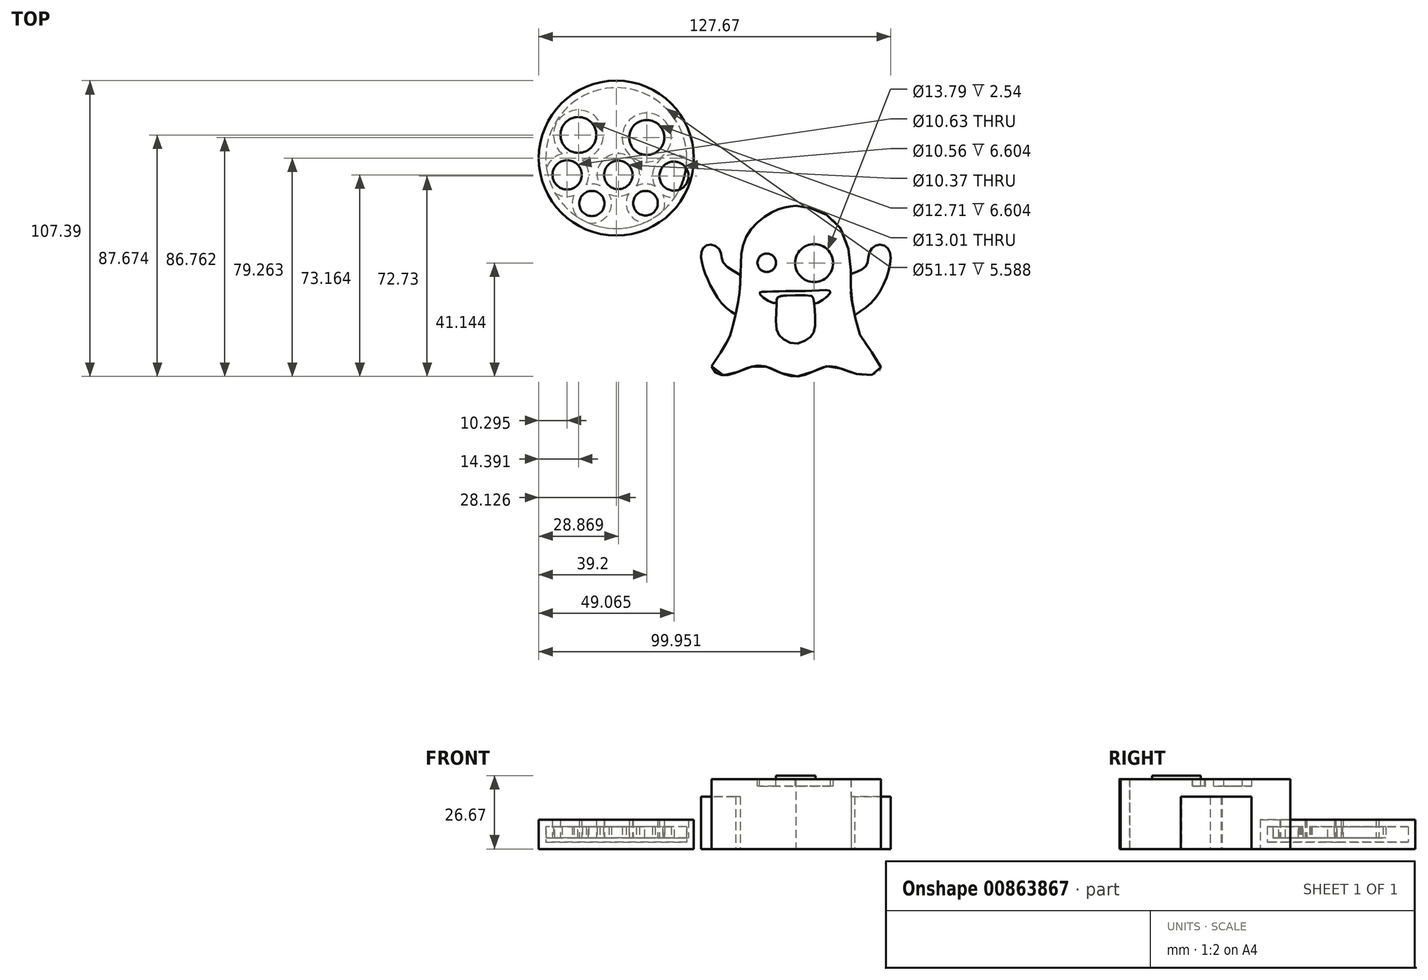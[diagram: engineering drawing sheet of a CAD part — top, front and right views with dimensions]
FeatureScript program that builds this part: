
annotation { "Feature Type Name" : "Feature", "Feature Type Description" : "" }
export const myFeature = defineFeature(function(context is Context, id is Id, definition is map)
    precondition{}
    {
        {
            var Q0;
            Q0=qCreatedBy(makeId("Top.planeOp"),FACE);
            var sketch = newSketch(context, id + "F0", { "sketchPlane" : qUnion([Q0])});
            skFitSpline(sketch, "E0", {"points": [v(0, 33.37) * mm, v(-7.03, 31.69) * mm, v(-18.14, 21.85) * mm, v(-20.2, 4.64) * mm, v(-22.78, -10) * mm, v(-30.58, -24.95) * mm], "startDerivative": vector(-46.08, -6.92) * mm, "endDerivative": vector(-91.46, -132.61) * mm});
            skFitSpline(sketch, "E1", {"points": [v(-30.58, -24.95) * mm, v(-24.72, -28.16) * mm, v(-17.9, -25.74) * mm, v(-11.49, -24.95) * mm, v(-3.25, -28.24) * mm, v(4.42, -27.74) * mm, v(11.56, -24.95) * mm, v(18.87, -26.78) * mm, v(26.52, -28.24) * mm, v(30.85, -25.7) * mm, v(24.56, -15.85) * mm, v(21.42, -6.6) * mm, v(19.97, 1.7) * mm, v(19.99, 10.33) * mm, v(16.2, 25.2) * mm, v(7.47, 31.76) * mm, v(0, 33.37) * mm], "startDerivative": vector(37.88, -163.37) * mm, "endDerivative": vector(-123.08, 14.96) * mm});
            skSolve(sketch);
        }
        {
            var Q0;
            Q0=qCreatedBy(makeId("Top.planeOp"),FACE);
            var sketch = newSketch(context, id + "F1", { "sketchPlane" : qUnion([Q0])});
            skFitSpline(sketch, "E2", {"points": [v(-21.85, -6.15) * mm, v(-26.36, -2.74) * mm, v(-31.05, 4.47) * mm, v(-33.33, 9.93) * mm, v(-34.41, 15.22) * mm, v(-33.1, 18.55) * mm, v(-30.03, 19.1) * mm, v(-27.33, 16.69) * mm, v(-26.58, 13.03) * mm, v(-20.15, 8.18) * mm], "startDerivative": vector(-39.33, 23.82) * mm, "endDerivative": vector(59.82, -33.24) * mm});
            skFitSpline(sketch, "E3", {"points": [v(19.95, 8.53) * mm, v(25.55, 11.56) * mm, v(26.72, 16.3) * mm, v(30.11, 19.2) * mm, v(33.6, 17.45) * mm, v(33.92, 10.81) * mm, v(29.03, 0) * mm, v(21.4, -6.39) * mm], "startDerivative": vector(50, 16.36) * mm, "endDerivative": vector(-46.71, -30.92) * mm});
            skFitSpline(sketch, "E4", {"points": [v(-20.15, 8.18) * mm, v(-20.72, -2.19) * mm, v(-21.85, -6.15) * mm], "startDerivative": vector(-0.33, -18.94) * mm, "endDerivative": vector(-3.29, -8.96) * mm});
            skFitSpline(sketch, "E5", {"points": [v(21.4, -6.39) * mm, v(19.95, 0.9) * mm, v(19.95, 8.53) * mm], "startDerivative": vector(-3.63, 14.56) * mm, "endDerivative": vector(0.73, 15.28) * mm});
            skSolve(sketch);
        }
        {
            var Q0;
            Q0=makeQuery(id+"F0.imprint","IMPRINT",FACE,{"disambiguationData":[TD([[makeQuery(id+"F0.imprint","IMPRINT",EDGE,{"derivedFrom":sQuery(id+"F0.wireOp",EDGE,"E0")}),1.0]])]});
            extrude(context, id + "F2", {"entities" : qUnion([Q0]), "depth" : 25.4 * mm, "offsetDistance" : 25.4 * mm});
        }
        {
            var Q0;
            Q0=makeQuery(id+"F1.imprint","IMPRINT",FACE,{"disambiguationData":[TD([[makeQuery(id+"F1.imprint","IMPRINT",EDGE,{"derivedFrom":sQuery(id+"F1.wireOp",EDGE,"E2")}),-1.0]])]});
            var Q1;
            Q1=makeQuery(id+"F1.imprint","IMPRINT",FACE,{"disambiguationData":[TD([[makeQuery(id+"F1.imprint","IMPRINT",EDGE,{"derivedFrom":sQuery(id+"F1.wireOp",EDGE,"E3")}),-1.0]])]});
            extrude(context, id + "F3", {"entities" : qUnion([Q0, Q1]), "operationType" : NewBodyOperationType.ADD, "depth" : 19.05 * mm, "offsetDistance" : 25.4 * mm});
        }
        {
            var Q0;
            Q0=makeQuery(id+"F2.opExtrude","CAP_FACE",FACE,{"disambiguationData":[OSD([sQuery(id+"F0.wireOp",EDGE,"E0"),sQuery(id+"F0.wireOp",EDGE,"E1")])],"isStart":false});
            cPlane(context, id + "F4", {"entities" : qUnion([Q0]), "cplaneType" : CPlaneType.OFFSET, "offset" : 0 * mm, "width" : 152.4 * mm, "height" : 152.4 * mm});
        }
        {
            var Q0;
            Q0=qCreatedBy(id+"F4.planeOp",FACE);
            var sketch = newSketch(context, id + "F5", { "sketchPlane" : qUnion([Q0])});
            skCircle(sketch, "E6", {"center": v(-10.56, 12.59) * mm, "radius": 3.36 * mm});
            skPoint(sketch, "E6.first.point", {"position": v(-10.47, 15.95) * mm});
            skPoint(sketch, "E6.second.point", {"position": v(-7.24, 12.05) * mm});
            skPoint(sketch, "E6.third.point", {"position": v(-13.31, 10.67) * mm});
            skCircle(sketch, "E7", {"center": v(6.64, 12.5) * mm, "radius": 6.9 * mm});
            skPoint(sketch, "E7.first.point", {"position": v(8.05, 19.25) * mm});
            skPoint(sketch, "E7.second.point", {"position": v(9.72, 6.32) * mm});
            skPoint(sketch, "E7.third.point", {"position": v(2.14, 7.27) * mm});
            skFitSpline(sketch, "E8", {"points": [v(-7.1, -1.98) * mm, v(-11.22, -0.48) * mm, v(-13.15, 1.73) * mm, v(-11.05, 2.08) * mm, v(-2.94, 2.3) * mm, v(6.38, 2.43) * mm, v(12.54, 2.23) * mm, v(10.16, -0.65) * mm, v(6.74, -2.14) * mm, v(6.37, -0.27) * mm, v(4.87, 0.67) * mm, v(-1.12, 0.7) * mm, v(-5.2, 0.53) * mm, v(-6.82, -0.43) * mm, v(-7.1, -1.98) * mm]});
            skSolve(sketch);
        }
        {
            var Q0;
            Q0=makeQuery(id+"F5.imprint","IMPRINT",FACE,{"disambiguationData":[TD([[makeQuery(id+"F5.imprint","IMPRINT",EDGE,{"derivedFrom":sQuery(id+"F5.wireOp",EDGE,"E8")}),-1.0]])]});
            var Q1;
            Q1=makeQuery(id+"F5.imprint","IMPRINT",FACE,{"disambiguationData":[TD([[makeQuery(id+"F5.imprint","IMPRINT",EDGE,{"derivedFrom":sQuery(id+"F5.wireOp",EDGE,"E6")}),1.0]])]});
            var Q2;
            Q2=makeQuery(id+"F5.imprint","IMPRINT",FACE,{"disambiguationData":[TD([[makeQuery(id+"F5.imprint","IMPRINT",EDGE,{"derivedFrom":sQuery(id+"F5.wireOp",EDGE,"E7")}),1.0]])]});
            extrude(context, id + "F6", {"entities" : qUnion([Q0, Q1, Q2]), "operationType" : NewBodyOperationType.REMOVE, "oppositeDirection" : true, "depth" : 2.54 * mm, "offsetDistance" : 25.4 * mm});
        }
        {
            var Q0;
            Q0=qCreatedBy(id+"F4.planeOp",FACE);
            var sketch = newSketch(context, id + "F7", { "sketchPlane" : qUnion([Q0])});
            skFitSpline(sketch, "E9", {"points": [v(-6.94, -0.73) * mm, v(-7.05, -3.68) * mm, v(-7.05, -11.45) * mm, v(-5.12, -14.66) * mm, v(-0.42, -16.77) * mm, v(4.76, -14.74) * mm, v(6.66, -12.2) * mm, v(7, -6.3) * mm, v(6.52, -1.68) * mm, v(6.3, 0) * mm, v(5.1, 0.7) * mm, v(-2.98, 0.72) * mm, v(-5.26, 0.47) * mm, v(-6.66, 0) * mm, v(-6.94, -0.73) * mm]});
            skSolve(sketch);
        }
        {
            var Q0;
            Q0=makeQuery(id+"F7.imprint","IMPRINT",FACE,{"disambiguationData":[TD([[makeQuery(id+"F7.imprint","IMPRINT",EDGE,{"derivedFrom":sQuery(id+"F7.wireOp",EDGE,"E9")}),1.0]])]});
            extrude(context, id + "F8", {"entities" : qUnion([Q0]), "operationType" : NewBodyOperationType.ADD, "depth" : 1.27 * mm, "offsetDistance" : 25.4 * mm});
        }
        {
            var Q0;
            Q0=qCreatedBy(makeId("Top.planeOp"),FACE);
            var sketch = newSketch(context, id + "F9", { "sketchPlane" : qUnion([Q0])});
            skCircle(sketch, "E10", {"center": v(-65.18, 50.61) * mm, "radius": 28.12 * mm});
            skSolve(sketch);
        }
        {
            var Q0;
            Q0=makeQuery(id+"F9.imprint","IMPRINT",FACE,{"disambiguationData":[TD([[makeQuery(id+"F9.imprint","IMPRINT",EDGE,{"derivedFrom":sQuery(id+"F9.wireOp",EDGE,"E10")}),1.0]])]});
            extrude(context, id + "F10", {"entities" : qUnion([Q0]), "depth" : 4.06 * mm, "offsetDistance" : 25.4 * mm});
        }
        {
            var Q0;
            Q0=makeQuery(id+"F10.opExtrude","CAP_FACE",FACE,{"disambiguationData":[OSD([sQuery(id+"F9.wireOp",EDGE,"E10")])],"isStart":false});
            var sketch = newSketch(context, id + "F11", { "sketchPlane" : qUnion([Q0])});
            skCircle(sketch, "E11", {"center": v(-78.92, 59.02) * mm, "radius": 6.5 * mm});
            skCircle(sketch, "E12", {"center": v(-54.1, 58.11) * mm, "radius": 6.36 * mm});
            skCircle(sketch, "E13", {"center": v(-64.44, 44.51) * mm, "radius": 5.18 * mm});
            skCircle(sketch, "E14", {"center": v(-44.24, 44.08) * mm, "radius": 5.28 * mm});
            skCircle(sketch, "E15", {"center": v(-83.01, 44.51) * mm, "radius": 5.32 * mm});
            skCircle(sketch, "E16", {"center": v(-74.03, 34.12) * mm, "radius": 4.57 * mm});
            skCircle(sketch, "E17", {"center": v(-54.58, 34.23) * mm, "radius": 4.47 * mm});
            skSolve(sketch);
        }
        {
            var Q0;
            Q0=makeQuery(id+"F11.imprint","IMPRINT",FACE,{"disambiguationData":[TD([[makeQuery(id+"F11.imprint","IMPRINT",EDGE,{"derivedFrom":sQuery(id+"F11.wireOp",EDGE,"E11")}),-1.0]])]});
            extrude(context, id + "F12", {"entities" : qUnion([Q0]), "operationType" : NewBodyOperationType.ADD, "depth" : 6.6 * mm, "offsetDistance" : 25.4 * mm});
        }
        {
            var Q0;
            Q0=makeQuery(id+"F12.boolean.opBoolean","SPLIT",FACE,{"disambiguationData":[TD([makeQuery(id+"F12.opExtrude","SWEPT_FACE",FACE,{"disambiguationData":[OSD([sQuery(id+"F11.wireOp",EDGE,"E11")])]})])],"derivedFrom":makeQuery(id+"F10.opExtrude","CAP_FACE",FACE,{"disambiguationData":[OSD([sQuery(id+"F9.wireOp",EDGE,"E10")])],"isStart":false})});
            var Q1;
            Q1=makeQuery(id+"F12.boolean.opBoolean","SPLIT",FACE,{"disambiguationData":[TD([makeQuery(id+"F12.opExtrude","SWEPT_FACE",FACE,{"disambiguationData":[OSD([sQuery(id+"F11.wireOp",EDGE,"E12")])]})])],"derivedFrom":makeQuery(id+"F10.opExtrude","CAP_FACE",FACE,{"disambiguationData":[OSD([sQuery(id+"F9.wireOp",EDGE,"E10")])],"isStart":false})});
            var Q2;
            Q2=makeQuery(id+"F12.boolean.opBoolean","SPLIT",FACE,{"disambiguationData":[TD([makeQuery(id+"F12.opExtrude","SWEPT_FACE",FACE,{"disambiguationData":[OSD([sQuery(id+"F11.wireOp",EDGE,"E13")])]})])],"derivedFrom":makeQuery(id+"F10.opExtrude","CAP_FACE",FACE,{"disambiguationData":[OSD([sQuery(id+"F9.wireOp",EDGE,"E10")])],"isStart":false})});
            var Q3;
            Q3=makeQuery(id+"F12.boolean.opBoolean","SPLIT",FACE,{"disambiguationData":[TD([makeQuery(id+"F12.opExtrude","SWEPT_FACE",FACE,{"disambiguationData":[OSD([sQuery(id+"F11.wireOp",EDGE,"E15")])]})])],"derivedFrom":makeQuery(id+"F10.opExtrude","CAP_FACE",FACE,{"disambiguationData":[OSD([sQuery(id+"F9.wireOp",EDGE,"E10")])],"isStart":false})});
            var Q4;
            Q4=makeQuery(id+"F12.boolean.opBoolean","SPLIT",FACE,{"disambiguationData":[TD([makeQuery(id+"F12.opExtrude","SWEPT_FACE",FACE,{"disambiguationData":[OSD([sQuery(id+"F11.wireOp",EDGE,"E16")])]})])],"derivedFrom":makeQuery(id+"F10.opExtrude","CAP_FACE",FACE,{"disambiguationData":[OSD([sQuery(id+"F9.wireOp",EDGE,"E10")])],"isStart":false})});
            var Q5;
            Q5=makeQuery(id+"F12.boolean.opBoolean","SPLIT",FACE,{"disambiguationData":[TD([makeQuery(id+"F12.opExtrude","SWEPT_FACE",FACE,{"disambiguationData":[OSD([sQuery(id+"F11.wireOp",EDGE,"E17")])]})])],"derivedFrom":makeQuery(id+"F10.opExtrude","CAP_FACE",FACE,{"disambiguationData":[OSD([sQuery(id+"F9.wireOp",EDGE,"E10")])],"isStart":false})});
            var Q6;
            Q6=makeQuery(id+"F12.boolean.opBoolean","SPLIT",FACE,{"disambiguationData":[TD([makeQuery(id+"F12.opExtrude","SWEPT_FACE",FACE,{"disambiguationData":[OSD([sQuery(id+"F11.wireOp",EDGE,"E14")])]})])],"derivedFrom":makeQuery(id+"F10.opExtrude","CAP_FACE",FACE,{"disambiguationData":[OSD([sQuery(id+"F9.wireOp",EDGE,"E10")])],"isStart":false})});
            shell(context, id + "F13", {"entities" : qUnion([Q0, Q1, Q2, Q3, Q4, Q5, Q6]), "thickness" : 2.54 * mm});
        }
    });
